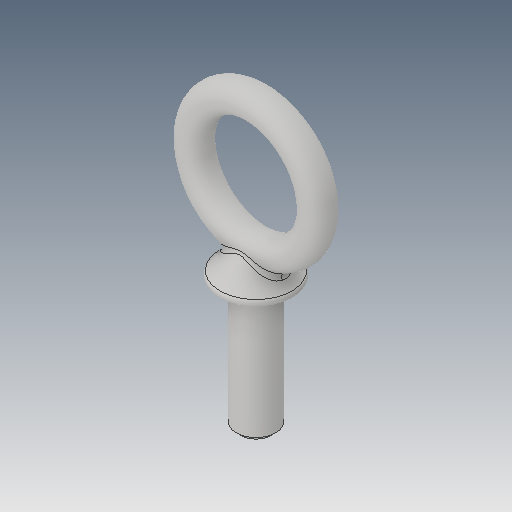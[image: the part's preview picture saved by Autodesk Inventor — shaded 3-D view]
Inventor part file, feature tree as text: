
AUTODESK INVENTOR PART (.ipt)
format: ipt  version: 2023.5 (Build 275446000, 446)  size: 205,824 bytes
history: native  units: in
note: dims shown in document units (in); Inventor stores cm internally (conversion verified against a paired STEP export)
features: fillet x1
ambient origin geometry x8: Origin, YZ Plane, XZ Plane, XY Plane, X Axis, Y Axis, Z Axis, Center Point
bodies: Solid1 (feature_tree)
feature tree (1):
  fillet  "Fillet1"  [1 undecoded]
note: 1 required parameter value undecoded (feature->parameter linkage not recoverable at this tier; creation-order binding heuristic only, values carry confidence <= 0.55)
